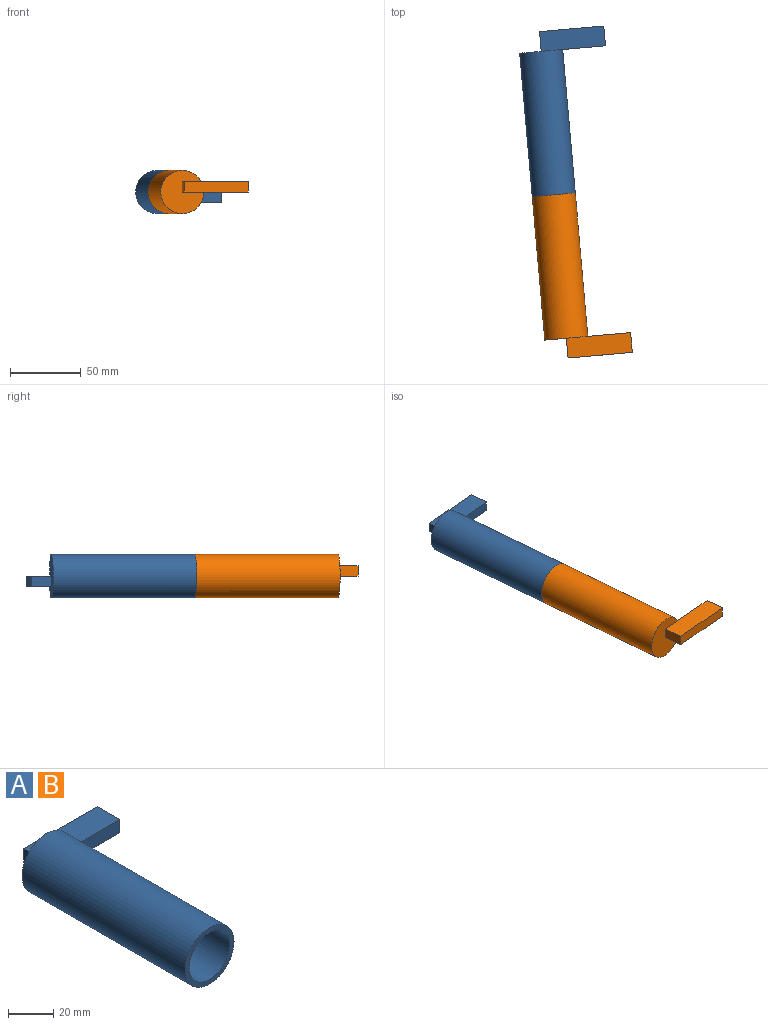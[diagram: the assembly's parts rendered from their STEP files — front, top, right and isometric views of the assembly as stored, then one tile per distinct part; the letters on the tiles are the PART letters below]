
ASSEMBLY  parts=2 mates=1
PART A: 11 faces, bbox 60.8x115.6x30.5 mm
  f0: cylinder r=15.24mm len=101.6mm, axis (0,1,0), area 9728.8mm2, adj f1,f2,f9
  f1: plane 30.48x30.48mm, normal (0,-1,0), area 223mm2, adj f0,f3
  f2: plane 30.48x30.48mm, normal (0,1,0), area 624.7mm2, adj f0,f5,f6,f7
  f3: cylinder r=12.7mm len=99.06mm, axis (0,1,0), area 7904.6mm2, adj f1,f4
  f4: plane 25.4x25.4mm, normal (0,-1,0), area 506.7mm2, adj f3
  f5: plane 45.53x14mm, normal (0,0,-1), area 637.3mm2, adj f2,f6,f8,f9,f10
  f6: plane 14x7.16mm, normal (-1,0,0), area 100.2mm2, adj f2,f5,f7,f10
  f7: plane 45.53x14mm, normal (0,0,1), area 637.3mm2, adj f2,f6,f8,f9,f10
  f8: plane 14x7.16mm, normal (1,0,0), area 100.2mm2, adj f5,f7,f9,f10
  f9: plane 32.08x7.16mm, normal (0,-1,0), area 221.1mm2, adj f0,f5,f7,f8
  f10: plane 45.53x7.16mm, normal (0,1,0), area 326.1mm2, adj f5,f6,f7,f8
PART B: same geometry as A
PLACE A rot(axis=(0,0,1),5deg) t=(-17.53,-14.84,-16.61)mm
PLACE B rot(axis=(1,0.04,0),180deg) t=(0.18,-217.26,-16.61)mm
MATE slider B.f0 <-> A.f0  axis (0.09,-1,0) through (-8.68,-116.05,-16.61)mm
